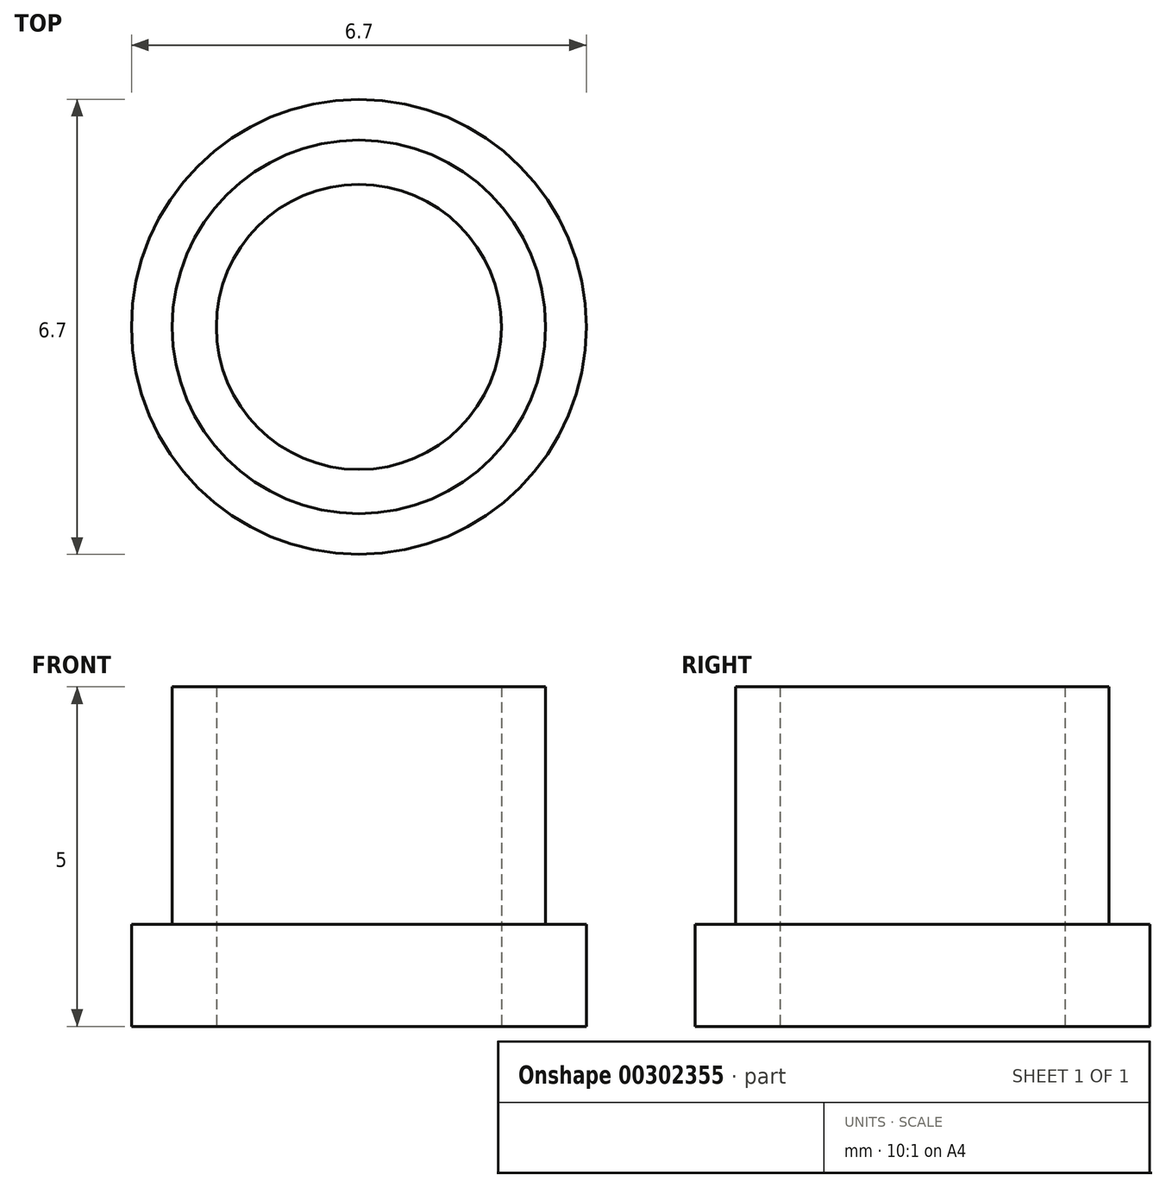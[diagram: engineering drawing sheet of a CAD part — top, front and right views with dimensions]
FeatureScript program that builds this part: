
annotation { "Feature Type Name" : "Feature", "Feature Type Description" : "" }
export const myFeature = defineFeature(function(context is Context, id is Id, definition is map)
    precondition{}
    {
        {
            var Q0;
            Q0=qCreatedBy(makeId("Front.planeOp"),FACE);
            var sketch = newSketch(context, id + "F0", { "sketchPlane" : qUnion([Q0])});
            skLineSegment(sketch, "E0", {"start": v(-2.1, 0) * mm, "end": v(-2.1, 5) * mm});
            skLineSegment(sketch, "E1", {"start": v(-2.1, 5) * mm, "end": v(-2.75, 5) * mm});
            skLineSegment(sketch, "E2", {"start": v(-2.75, 5) * mm, "end": v(-2.75, 1.5) * mm});
            skLineSegment(sketch, "E3", {"start": v(-2.75, 1.5) * mm, "end": v(-3.35, 1.5) * mm});
            skLineSegment(sketch, "E4", {"start": v(-3.35, 1.5) * mm, "end": v(-3.35, 0) * mm});
            skLineSegment(sketch, "E5", {"start": v(-3.35, 0) * mm, "end": v(-2.1, 0) * mm});
            skLineSegment(sketch, "E6", {"start": v(0, 0) * mm, "end": v(0, 5) * mm, "construction": true});
            skLineSegment(sketch, "E7.MirrorCS", {"start": v(2.1, 0) * mm, "end": v(2.1, 5) * mm});
            skLineSegment(sketch, "E8.MirrorCS", {"start": v(2.1, 5) * mm, "end": v(2.75, 5) * mm});
            skLineSegment(sketch, "E9.MirrorCS", {"start": v(2.75, 5) * mm, "end": v(2.75, 1.5) * mm});
            skLineSegment(sketch, "E10.MirrorCS", {"start": v(2.75, 1.5) * mm, "end": v(3.35, 1.5) * mm});
            skLineSegment(sketch, "E11.MirrorCS", {"start": v(3.35, 1.5) * mm, "end": v(3.35, 0) * mm});
            skLineSegment(sketch, "E12.MirrorCS", {"start": v(3.35, 0) * mm, "end": v(2.1, 0) * mm});
            skSolve(sketch);
        }
        {
            var Q0;
            Q0=makeQuery(id+"F0.imprint","IMPRINT",FACE,{"disambiguationData":[TD([[makeQuery(id+"F0.imprint","IMPRINT",EDGE,{"derivedFrom":sQuery(id+"F0.wireOp",EDGE,"E0")}),1.0]])]});
            var Q1;
            Q1=sQuery(id+"F0.wireOp",EDGE,"E6");
            revolve(context, id + "F1", {"entities" : qUnion([Q0]), "axis" : qUnion([Q1]), "revolveType" : RevolveType.FULL});
        }
    });
